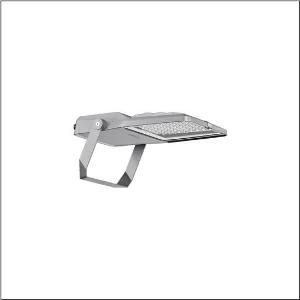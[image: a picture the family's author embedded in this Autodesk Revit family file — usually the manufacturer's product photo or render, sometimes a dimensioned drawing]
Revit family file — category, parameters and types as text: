
# Revit family: floodlight_fl_21_iq_mini___pl52_5xa7772d4d1a_6062
name_source: partatom
category: Lighting Fixtures
units: mm (PartAtom-declared; Revit-internal decimal feet)

## family parameters
Cut with Voids When Loaded = No
Host = Face
Light Source = No
Part Type = Normal
Room Calculation Point = No
Round Connector Dimension = Use Diameter
Shared = No

## types (1)
- --- (1 x LED, 18610 lm, 143 W, 4000K)
    Apparent Load = 143 VA
    CIE Flux Codes = 26 60 98 100 100
    Color Rendering = 70
    Color Temperature = 4000K
    Default Elevation = 1800 mm
    Description = Floodlight FL 21 iQ mini, floodlight, primary light control with lens, of PMMA, primary optical cover: protective disc, of toughened safety glass, transparent, light distribution: PL52, light emission: direct distribution, installation type: surface-mounted, LED, High Power LED, rated luminous flux: 18.610lm, luminous efficacy: 130lm/W, light colour: 740, colour temperature: 4000K, control: Street-Remote, Auto-Match, Temp-Guard, Night-Set, Smart-Wire, Desk-Remote (wireless, voltage-free reading and setting of iQ features in the workshop via application-optimized NFC function/RFID function), optimised constant luminous flux control (CLO 2.0), with terminal, 6-pole, mains connection: 220..240V, AC, 50/60Hz, start of lifetime: 143W, end of service life: 152W, reduction: 61W, luminaire housing, of diecast aluminium, powder-coated, Siteco® metallic grey (DB 702S), corrosivity category C5 mid according to DIN EN ISO 12944, sealing non-destructively replaceable, mounting bracket, of steel, galvanised, powder-coated, Siteco® metallic grey (DB 702S), protection rating (complete): IP66, insulation class (complete): insulation class II (safety insulation), certification: CE, ENEC, VDE, protection symbol: D, impact resistance: IK08, permissible operating ambient temperature: -40..+40°C, permissible operating ambient temperature for outdoor applications: -40..+50°C, standard: DIN EN 12944, LABS conformity tested according to VDMA 24364:2018-05, packaging unit: 1 piece

Light Distribution: PL52
    Height = 70 mm
    Lamp = 1 x LED
    Lamp Light Flux = 18610 lm
    Lamp Power = 143 W
    Lamp count = 1
    Length = 485 mm
    Luminous efficacy = 130 lm/W
    Manufacturer = Siteco
    ModVariant = No
    Model = 5XA7772D4D1A
    Number of Poles = 1
    OnlyDefault = Yes
    Power Factor = 1
    Product Name = Floodlight FL 21 iQ mini | PL52
    Product group = floodlight | pylon annexe
    ProductGroupID = 6200
    Protection Class = Protection class II
    Protection Degree = IP 66
    RLX_Detail_Level = 1
    RLX_Emergency_Light_Flux = 0 lm
    RLX_Emergency_Type = 0
    RLX_Emergency_Type_DB = No
    RlxData = <blob elided: 96693 chars, md5=7376ef65>
    Socket = socket
    Standby Power = 0 W
    System Light Flux = 18610 lm
    System Power = 143 W
    Type Comments = factory setting: luminous flux: 100 % | dim-lin: 254 | 730 mA
    Type Image = l_1006845.jpg
    URL = http://relux.com
    VarID = @adj_095935
    Voltage = 0 V
    Weight = 0.00 kg
    Width = 337 mm

## geometry (parser evidence)
native form markers: Blend x4, Sweep x11
no freeform markers — native parametric forms only
